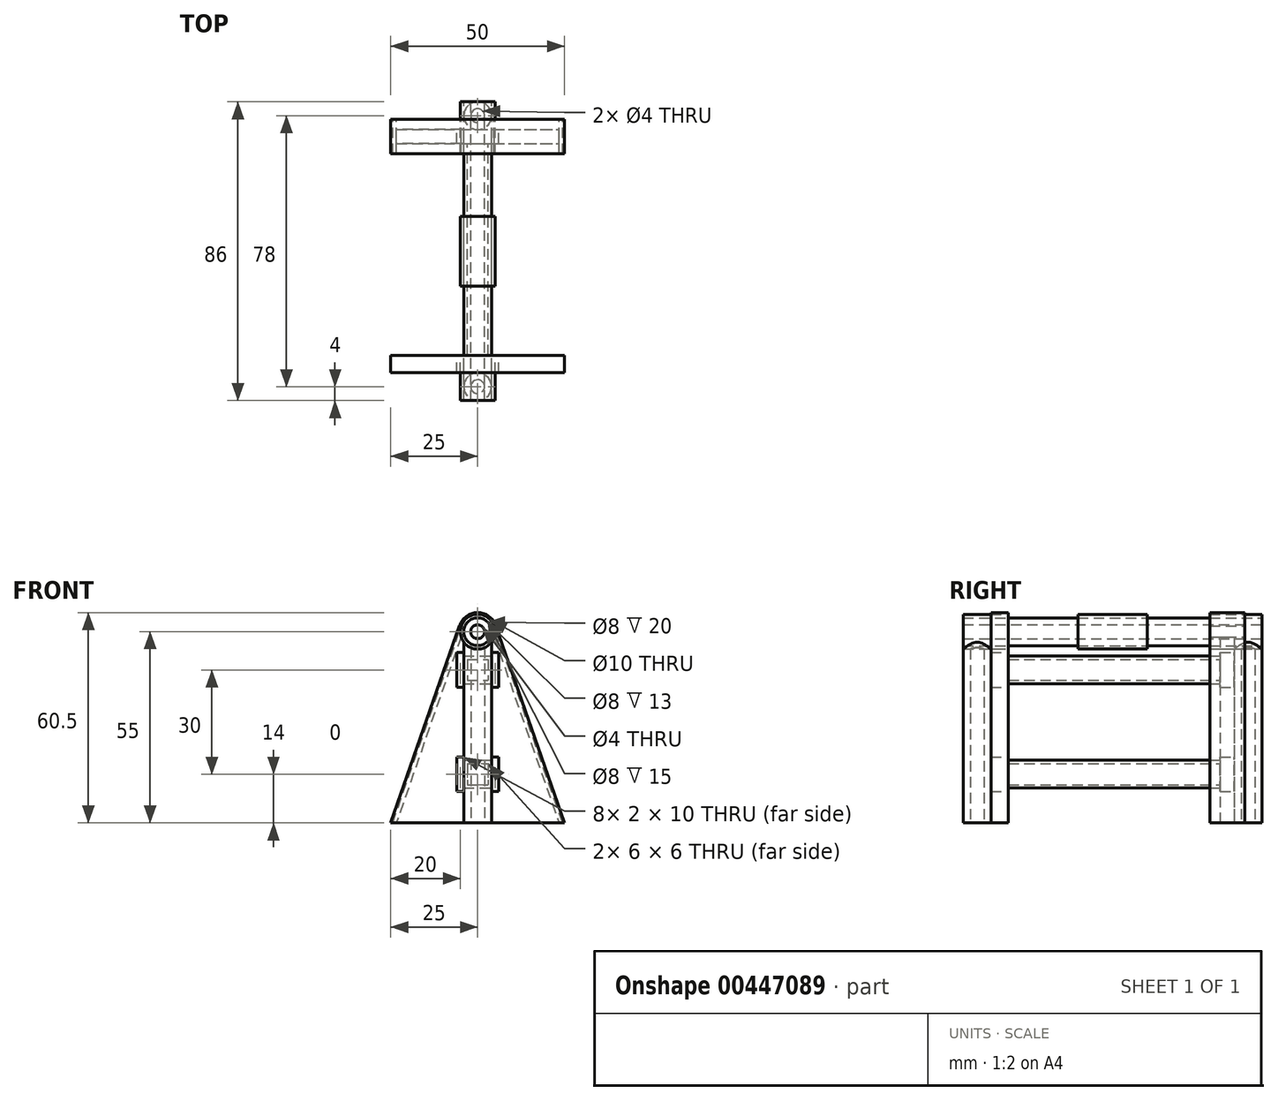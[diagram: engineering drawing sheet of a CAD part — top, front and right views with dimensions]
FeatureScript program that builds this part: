
annotation { "Feature Type Name" : "Feature", "Feature Type Description" : "" }
export const myFeature = defineFeature(function(context is Context, id is Id, definition is map)
    precondition{}
    {
        {
            var Q0;
            Q0=qCreatedBy(makeId("Top.planeOp"),FACE);
            var sketch = newSketch(context, id + "F0", { "sketchPlane" : qUnion([Q0])});
            skCircle(sketch, "E0", {"center": v(0, -4) * mm, "radius": 4 * mm});
            skCircle(sketch, "E1", {"center": v(0, -82) * mm, "radius": 4 * mm});
            skCircle(sketch, "E2", {"center": v(0, -4) * mm, "radius": 2 * mm});
            skCircle(sketch, "E3", {"center": v(0, -82) * mm, "radius": 2 * mm});
            skSolve(sketch);
        }
        {
            var Q0;
            Q0=qCreatedBy(makeId("Front.planeOp"),FACE);
            var sketch = newSketch(context, id + "F1", { "sketchPlane" : qUnion([Q0])});
            skCircle(sketch, "E4", {"center": v(0, 55) * mm, "radius": 4 * mm});
            skCircle(sketch, "E5", {"center": v(0, 55) * mm, "radius": 5 * mm});
            skLineSegment(sketch, "E6", {"start": v(-25, 0) * mm, "end": v(25, 0) * mm});
            skLineSegment(sketch, "E7.bottom", {"start": v(-4, 48) * mm, "end": v(4, 48) * mm});
            skLineSegment(sketch, "E7.top", {"start": v(-4, 40) * mm, "end": v(4, 40) * mm});
            skLineSegment(sketch, "E7.left", {"start": v(-4, 48) * mm, "end": v(-4, 40) * mm});
            skLineSegment(sketch, "E7.right", {"start": v(4, 48) * mm, "end": v(4, 40) * mm});
            skLineSegment(sketch, "E8.bottom", {"start": v(-3, 47) * mm, "end": v(3, 47) * mm});
            skLineSegment(sketch, "E8.top", {"start": v(-3, 41) * mm, "end": v(3, 41) * mm});
            skLineSegment(sketch, "E8.left", {"start": v(-3, 47) * mm, "end": v(-3, 41) * mm});
            skLineSegment(sketch, "E8.right", {"start": v(3, 47) * mm, "end": v(3, 41) * mm});
            skLineSegment(sketch, "E9", {"start": v(3, 41) * mm, "end": v(4, 41) * mm, "construction": true});
            skLineSegment(sketch, "E10", {"start": v(3, 41) * mm, "end": v(3, 40) * mm, "construction": true});
            skPoint(sketch, "E11", {"position": v(0, 44) * mm});
            skLineSegment(sketch, "E12.bottom", {"start": v(-4, 18) * mm, "end": v(4, 18) * mm});
            skLineSegment(sketch, "E12.top", {"start": v(-4, 10) * mm, "end": v(4, 10) * mm});
            skLineSegment(sketch, "E12.left", {"start": v(-4, 18) * mm, "end": v(-4, 10) * mm});
            skLineSegment(sketch, "E12.right", {"start": v(4, 18) * mm, "end": v(4, 10) * mm});
            skLineSegment(sketch, "E13.bottom", {"start": v(-3, 17) * mm, "end": v(3, 17) * mm});
            skLineSegment(sketch, "E13.top", {"start": v(-3, 11) * mm, "end": v(3, 11) * mm});
            skLineSegment(sketch, "E13.left", {"start": v(-3, 17) * mm, "end": v(-3, 11) * mm});
            skLineSegment(sketch, "E13.right", {"start": v(3, 17) * mm, "end": v(3, 11) * mm});
            skLineSegment(sketch, "E14", {"start": v(3, 11) * mm, "end": v(4, 11) * mm, "construction": true});
            skLineSegment(sketch, "E15", {"start": v(3, 11) * mm, "end": v(3, 10) * mm, "construction": true});
            skPoint(sketch, "E16", {"position": v(0, 14) * mm});
            skLineSegment(sketch, "E17", {"start": v(4, 52) * mm, "end": v(4, 0) * mm, "construction": true});
            skLineSegment(sketch, "E18", {"start": v(-4, 52) * mm, "end": v(-4, 0) * mm, "construction": true});
            skCircle(sketch, "E19", {"center": v(0, 55) * mm, "radius": 3 * mm});
            skCircle(sketch, "E20", {"center": v(0, 55) * mm, "radius": 5.5 * mm});
            skLineSegment(sketch, "E21", {"start": v(-25, 0) * mm, "end": v(-5.2, 56.81) * mm});
            skLineSegment(sketch, "E22", {"start": v(25, 0) * mm, "end": v(5.2, 56.81) * mm});
            skLineSegment(sketch, "E23.bottom", {"start": v(-4, 39) * mm, "end": v(-6, 39) * mm});
            skLineSegment(sketch, "E23.top", {"start": v(-4, 49) * mm, "end": v(-6, 49) * mm});
            skLineSegment(sketch, "E23.left", {"start": v(-4, 39) * mm, "end": v(-4, 49) * mm});
            skLineSegment(sketch, "E23.right", {"start": v(-6, 39) * mm, "end": v(-6, 49) * mm});
            skLineSegment(sketch, "E24", {"start": v(0, 55) * mm, "end": v(0, 0) * mm, "construction": true});
            skLineSegment(sketch, "E25.MirrorCS", {"start": v(4, 39) * mm, "end": v(6, 39) * mm});
            skLineSegment(sketch, "E26.MirrorCS", {"start": v(4, 49) * mm, "end": v(6, 49) * mm});
            skLineSegment(sketch, "E27.MirrorCS", {"start": v(6, 39) * mm, "end": v(6, 49) * mm});
            skLineSegment(sketch, "E28.MirrorCS", {"start": v(4, 39) * mm, "end": v(4, 49) * mm});
            skLineSegment(sketch, "E29.bottom", {"start": v(-4, 9) * mm, "end": v(-6, 9) * mm});
            skLineSegment(sketch, "E29.top", {"start": v(-4, 19) * mm, "end": v(-6, 19) * mm});
            skLineSegment(sketch, "E29.left", {"start": v(-4, 9) * mm, "end": v(-4, 19) * mm});
            skLineSegment(sketch, "E29.right", {"start": v(-6, 9) * mm, "end": v(-6, 19) * mm});
            skLineSegment(sketch, "E30.MirrorCS", {"start": v(4, 9) * mm, "end": v(6, 9) * mm});
            skLineSegment(sketch, "E31.MirrorCS", {"start": v(6, 9) * mm, "end": v(6, 19) * mm});
            skLineSegment(sketch, "E32.MirrorCS", {"start": v(4, 19) * mm, "end": v(6, 19) * mm});
            skLineSegment(sketch, "E33.MirrorCS", {"start": v(4, 9) * mm, "end": v(4, 19) * mm});
            skCircle(sketch, "E34", {"center": v(0, 55) * mm, "radius": 2 * mm});
            skLineSegment(sketch, "E35", {"start": v(-24.47, 0) * mm, "end": v(-4.72, 56.65) * mm});
            skLineSegment(sketch, "E36", {"start": v(-4.76, 53.48) * mm, "end": v(-23.41, 0) * mm});
            skLineSegment(sketch, "E37", {"start": v(-17.97, 18.64) * mm, "end": v(-17.03, 18.3) * mm, "construction": true});
            skLineSegment(sketch, "E38.MirrorCS", {"start": v(4.76, 53.48) * mm, "end": v(23.41, 0) * mm});
            skLineSegment(sketch, "E39.MirrorCS", {"start": v(24.47, 0) * mm, "end": v(4.72, 56.65) * mm});
            skSolve(sketch);
        }
        {
            var Q0;
            Q0=makeQuery(id+"F1.imprint","IMPRINT",FACE,{"disambiguationData":[TD([[makeQuery(id+"F1.imprint","IMPRINT",EDGE,{"derivedFrom":sQuery(id+"F1.wireOp",EDGE,"E7.bottom")}),-1.0]])]});
            var Q1;
            Q1=makeQuery(id+"F1.imprint","IMPRINT",FACE,{"disambiguationData":[TD([[makeQuery(id+"F1.imprint","IMPRINT",EDGE,{"derivedFrom":sQuery(id+"F1.wireOp",EDGE,"E12.bottom")}),-1.0]])]});
            var Q2;
            {var subQ5=sQuery(id+"F1.wireOp",EDGE,"E7.top");Q2=makeQuery(id+"F1.imprint","IMPRINT",FACE,{"disambiguationData":[TD([[makeQuery(id+"F1.imprint","IMPRINT",EDGE,{"derivedFrom":subQ5}),1.0]])]});}
            extrude(context, id + "F2", {"entities" : qUnion([Q0, Q1, Q2]), "depth" : 73 * mm, "hasSecondDirection" : true, "secondDirectionOppositeDirection" : false, "secondDirectionDepth" : 12 * mm});
        }
        {
            var Q0;
            Q0=makeQuery(id+"F0.imprint","IMPRINT",FACE,{"disambiguationData":[TD([[makeQuery(id+"F0.imprint","IMPRINT",EDGE,{"derivedFrom":sQuery(id+"F0.wireOp",EDGE,"E2")}),1.0]])]});
            var Q1;
            Q1=makeQuery(id+"F0.imprint","IMPRINT",FACE,{"disambiguationData":[TD([[makeQuery(id+"F0.imprint","IMPRINT",EDGE,{"derivedFrom":sQuery(id+"F0.wireOp",EDGE,"E0")}),1.0]])]});
            var Q2;
            Q2=makeQuery(id+"F0.imprint","IMPRINT",FACE,{"disambiguationData":[TD([[makeQuery(id+"F0.imprint","IMPRINT",EDGE,{"derivedFrom":sQuery(id+"F0.wireOp",EDGE,"E1")}),1.0]])]});
            var Q3;
            Q3=makeQuery(id+"F0.imprint","IMPRINT",FACE,{"disambiguationData":[TD([[makeQuery(id+"F0.imprint","IMPRINT",EDGE,{"derivedFrom":sQuery(id+"F0.wireOp",EDGE,"E3")}),1.0]])]});
            extrude(context, id + "F3", {"entities" : qUnion([Q0, Q1, Q2, Q3]), "operationType" : NewBodyOperationType.REMOVE, "depth" : 50 * mm});
        }
        {
            var Q0;
            Q0=qSketchRegion(id+"F0",true);
            extrude(context, id + "F4", {"entities" : qUnion([Q0]), "depth" : 55 * mm});
        }
        {
            var Q0;
            Q0=makeQuery(id+"F1.imprint","IMPRINT",FACE,{"disambiguationData":[TD([[makeQuery(id+"F1.imprint","IMPRINT",EDGE,{"derivedFrom":sQuery(id+"F1.wireOp",EDGE,"E4")}),1.0]])]});
            var Q1;
            Q1=makeQuery(id+"F1.imprint","IMPRINT",FACE,{"disambiguationData":[TD([[makeQuery(id+"F1.imprint","IMPRINT",EDGE,{"derivedFrom":sQuery(id+"F1.wireOp",EDGE,"E4")}),-1.0]])]});
            var Q2;
            Q2=makeQuery(id+"F1.imprint","IMPRINT",FACE,{"disambiguationData":[TD([[makeQuery(id+"F1.imprint","IMPRINT",EDGE,{"derivedFrom":sQuery(id+"F1.wireOp",EDGE,"E19")}),1.0]])]});
            var Q3;
            Q3=makeQuery(id+"F1.imprint","IMPRINT",FACE,{"disambiguationData":[TD([[makeQuery(id+"F1.imprint","IMPRINT",EDGE,{"derivedFrom":sQuery(id+"F1.wireOp",EDGE,"E34")}),1.0]])]});
            extrude(context, id + "F5", {"entities" : qUnion([Q0, Q1, Q2, Q3]), "operationType" : NewBodyOperationType.REMOVE, "depth" : 120 * mm});
        }
        {
            var Q0;
            Q0=makeQuery(id+"F1.imprint","IMPRINT",FACE,{"disambiguationData":[TD([[makeQuery(id+"F1.imprint","IMPRINT",EDGE,{"derivedFrom":sQuery(id+"F1.wireOp",EDGE,"E4")}),-1.0]])]});
            extrude(context, id + "F6", {"entities" : qUnion([Q0]), "depth" : 15 * mm});
        }
        {
            var Q0;
            Q0=makeQuery(id+"F1.imprint","IMPRINT",FACE,{"disambiguationData":[TD([[makeQuery(id+"F1.imprint","IMPRINT",EDGE,{"derivedFrom":sQuery(id+"F1.wireOp",EDGE,"E4")}),-1.0]])]});
            var Q1;
            {var subQ0=sQuery(id+"F1.wireOp",EDGE,"NSQy4Wvw-krST-z6iW-aOdV-dfbufY4ojtwf");Q1=makeQuery(id+"F1.imprint","IMPRINT",FACE,{"disambiguationData":[TD([[makeQuery(id+"F1.imprint","IMPRINT",EDGE,{"derivedFrom":subQ0}),1.0]])]});}
            var Q2;
            {var subQ0=sQuery(id+"F1.wireOp",EDGE,"pC06kpPF-Ja5L-Bko1-UVUB-2QjUFd2QXtQQ");Q2=makeQuery(id+"F1.imprint","IMPRINT",FACE,{"disambiguationData":[TD([[makeQuery(id+"F1.imprint","IMPRINT",EDGE,{"derivedFrom":subQ0}),1.0]])]});}
            extrude(context, id + "F7", {"entities" : qUnion([Q0, Q1, Q2]), "depth" : 86 * mm, "hasSecondDirection" : true, "secondDirectionOppositeDirection" : false, "secondDirectionDepth" : 73 * mm});
        }
        {
            var Q0;
            Q0=makeQuery(id+"F1.imprint","IMPRINT",FACE,{"disambiguationData":[TD([[makeQuery(id+"F1.imprint","IMPRINT",EDGE,{"derivedFrom":sQuery(id+"F1.wireOp",EDGE,"E4")}),1.0]])]});
            var Q1;
            Q1=makeQuery(id+"F1.imprint","IMPRINT",FACE,{"disambiguationData":[TD([[makeQuery(id+"F1.imprint","IMPRINT",EDGE,{"derivedFrom":sQuery(id+"F1.wireOp",EDGE,"E19")}),1.0]])]});
            extrude(context, id + "F8", {"entities" : qUnion([Q0, Q1]), "depth" : 86 * mm});
        }
        {
            var Q0;
            {var subQ6=sQuery(id+"F1.wireOp",EDGE,"E7.bottom");Q0=makeQuery(id+"F1.imprint","IMPRINT",FACE,{"disambiguationData":[TD([[makeQuery(id+"F1.imprint","IMPRINT",EDGE,{"derivedFrom":subQ6}),1.0]])]});}
            var Q1;
            {var subQ0=sQuery(id+"F1.wireOp",EDGE,"E36");var subQ1=sQuery(id+"F1.wireOp",EDGE,"E5");var subQ2=makeQuery(id+"F1.imprint","INTERSECT",VERTEX,{"derivedFrom":[subQ1,subQ0]});Q1=makeQuery(id+"F1.imprint","IMPRINT",FACE,{"disambiguationData":[TD([[makeQuery(id+"F1.imprint","IMPRINT",EDGE,{"disambiguationData":[TD([[subQ2,-1.0]])],"derivedFrom":subQ1}),-1.0]])]});}
            var Q2;
            {var subQ1=sQuery(id+"F1.wireOp",EDGE,"E7.bottom");Q2=makeQuery(id+"F1.imprint","IMPRINT",FACE,{"disambiguationData":[TD([[makeQuery(id+"F1.imprint","IMPRINT",EDGE,{"derivedFrom":subQ1}),-1.0]])]});}
            var Q3;
            Q3=makeQuery(id+"F1.imprint","IMPRINT",FACE,{"disambiguationData":[TD([[makeQuery(id+"F1.imprint","IMPRINT",EDGE,{"derivedFrom":sQuery(id+"F1.wireOp",EDGE,"E8.bottom")}),-1.0]])]});
            var Q4;
            Q4=makeQuery(id+"F1.imprint","IMPRINT",FACE,{"disambiguationData":[TD([[makeQuery(id+"F1.imprint","IMPRINT",EDGE,{"derivedFrom":sQuery(id+"F1.wireOp",EDGE,"E13.bottom")}),-1.0]])]});
            var Q5;
            {var subQ1=sQuery(id+"F1.wireOp",EDGE,"E12.bottom");Q5=makeQuery(id+"F1.imprint","IMPRINT",FACE,{"disambiguationData":[TD([[makeQuery(id+"F1.imprint","IMPRINT",EDGE,{"derivedFrom":subQ1}),-1.0]])]});}
            extrude(context, id + "F9", {"entities" : qUnion([Q0, Q1, Q2, Q3, Q4, Q5]), "depth" : 12 * mm, "hasSecondDirection" : true, "secondDirectionOppositeDirection" : false, "secondDirectionDepth" : 8 * mm});
        }
        {
            var Q0;
            {var subQ1=sQuery(id+"F1.wireOp",EDGE,"E7.bottom");Q0=makeQuery(id+"F1.imprint","IMPRINT",FACE,{"disambiguationData":[TD([[makeQuery(id+"F1.imprint","IMPRINT",EDGE,{"derivedFrom":subQ1}),-1.0]])]});}
            var Q1;
            Q1=makeQuery(id+"F1.imprint","IMPRINT",FACE,{"disambiguationData":[TD([[makeQuery(id+"F1.imprint","IMPRINT",EDGE,{"derivedFrom":sQuery(id+"F1.wireOp",EDGE,"E6")}),1.0]])]});
            var Q2;
            Q2=makeQuery(id+"F1.imprint","IMPRINT",FACE,{"disambiguationData":[TD([[makeQuery(id+"F1.imprint","IMPRINT",EDGE,{"derivedFrom":sQuery(id+"F1.wireOp",EDGE,"E5")}),-1.0]])]});
            var Q3;
            {var subQ2=sQuery(id+"F1.wireOp",EDGE,"E35");var subQ4=sQuery(id+"F1.wireOp",EDGE,"E5");var subQ5=makeQuery(id+"F1.imprint","INTERSECT",VERTEX,{"derivedFrom":[subQ4,subQ2]});Q3=makeQuery(id+"F1.imprint","IMPRINT",FACE,{"disambiguationData":[TD([[makeQuery(id+"F1.imprint","IMPRINT",EDGE,{"disambiguationData":[TD([[subQ5,1.0]])],"derivedFrom":subQ4}),-1.0]])]});}
            var Q4;
            {var subQ6=sQuery(id+"F1.wireOp",EDGE,"E7.bottom");Q4=makeQuery(id+"F1.imprint","IMPRINT",FACE,{"disambiguationData":[TD([[makeQuery(id+"F1.imprint","IMPRINT",EDGE,{"derivedFrom":subQ6}),1.0]])]});}
            var Q5;
            Q5=makeQuery(id+"F1.imprint","IMPRINT",FACE,{"disambiguationData":[TD([[makeQuery(id+"F1.imprint","IMPRINT",EDGE,{"derivedFrom":sQuery(id+"F1.wireOp",EDGE,"E8.bottom")}),-1.0]])]});
            var Q6;
            Q6=makeQuery(id+"F1.imprint","IMPRINT",FACE,{"disambiguationData":[TD([[makeQuery(id+"F1.imprint","IMPRINT",EDGE,{"derivedFrom":sQuery(id+"F1.wireOp",EDGE,"E13.bottom")}),-1.0]])]});
            var Q7;
            {var subQ1=sQuery(id+"F1.wireOp",EDGE,"E12.bottom");Q7=makeQuery(id+"F1.imprint","IMPRINT",FACE,{"disambiguationData":[TD([[makeQuery(id+"F1.imprint","IMPRINT",EDGE,{"derivedFrom":subQ1}),-1.0]])]});}
            extrude(context, id + "F10", {"entities" : qUnion([Q0, Q1, Q2, Q3, Q4, Q5, Q6, Q7]), "depth" : 78 * mm, "hasSecondDirection" : true, "secondDirectionOppositeDirection" : false, "secondDirectionDepth" : 73 * mm});
        }
        {
            var Q0;
            Q0=makeQuery(id+"F1.imprint","IMPRINT",FACE,{"disambiguationData":[TD([[makeQuery(id+"F1.imprint","IMPRINT",EDGE,{"derivedFrom":sQuery(id+"F1.wireOp",EDGE,"E4")}),-1.0]])]});
            extrude(context, id + "F11", {"entities" : qUnion([Q0]), "depth" : 53 * mm, "hasSecondDirection" : true, "secondDirectionOppositeDirection" : false, "secondDirectionDepth" : 33 * mm});
        }
        {
            var Q0;
            {var subQ0=sQuery(id+"F1.wireOp",EDGE,"E35");var subQ1=sQuery(id+"F1.wireOp",EDGE,"E6");var subQ2=makeQuery(id+"F1.imprint","INTERSECT",VERTEX,{"derivedFrom":[subQ1,subQ0]});Q0=makeQuery(id+"F1.imprint","IMPRINT",FACE,{"disambiguationData":[TD([[makeQuery(id+"F1.imprint","IMPRINT",EDGE,{"disambiguationData":[TD([[subQ2,-1.0]])],"derivedFrom":subQ1}),1.0]])]});}
            var Q1;
            {var subQ0=sQuery(id+"F1.wireOp",EDGE,"E38.MirrorCS");var subQ1=sQuery(id+"F1.wireOp",EDGE,"E6");var subQ2=makeQuery(id+"F1.imprint","INTERSECT",VERTEX,{"derivedFrom":[subQ1,subQ0]});Q1=makeQuery(id+"F1.imprint","IMPRINT",FACE,{"disambiguationData":[TD([[makeQuery(id+"F1.imprint","IMPRINT",EDGE,{"disambiguationData":[TD([[subQ2,-1.0]])],"derivedFrom":subQ1}),1.0]])]});}
            var Q2;
            {var subQ0=sQuery(id+"F1.wireOp",EDGE,"E38.MirrorCS");var subQ1=sQuery(id+"F1.wireOp",EDGE,"E5");var subQ2=makeQuery(id+"F1.imprint","INTERSECT",VERTEX,{"derivedFrom":[subQ1,subQ0]});Q2=makeQuery(id+"F1.imprint","IMPRINT",FACE,{"disambiguationData":[TD([[makeQuery(id+"F1.imprint","IMPRINT",EDGE,{"disambiguationData":[TD([[subQ2,-1.0]])],"derivedFrom":subQ1}),-1.0]])]});}
            var Q3;
            {var subQ0=sQuery(id+"F1.wireOp",EDGE,"E35");var subQ1=sQuery(id+"F1.wireOp",EDGE,"E5");var subQ2=makeQuery(id+"F1.imprint","INTERSECT",VERTEX,{"derivedFrom":[subQ1,subQ0]});Q3=makeQuery(id+"F1.imprint","IMPRINT",FACE,{"disambiguationData":[TD([[makeQuery(id+"F1.imprint","IMPRINT",EDGE,{"disambiguationData":[TD([[subQ2,-1.0]])],"derivedFrom":subQ1}),-1.0]])]});}
            extrude(context, id + "F12", {"entities" : qUnion([Q0, Q1, Q2, Q3]), "depth" : 15 * mm, "hasSecondDirection" : true, "secondDirectionOppositeDirection" : false, "secondDirectionDepth" : 5 * mm});
        }
        {
            var Q0;
            {var subQ0=sQuery(id+"F1.wireOp",EDGE,"E22");Q0=makeQuery(id+"F1.imprint","IMPRINT",FACE,{"disambiguationData":[TD([[makeQuery(id+"F1.imprint","IMPRINT",EDGE,{"derivedFrom":subQ0}),1.0]])]});}
            var Q1;
            {var subQ2=sQuery(id+"F1.wireOp",EDGE,"E35");var subQ4=sQuery(id+"F1.wireOp",EDGE,"E5");var subQ5=makeQuery(id+"F1.imprint","INTERSECT",VERTEX,{"derivedFrom":[subQ4,subQ2]});Q1=makeQuery(id+"F1.imprint","IMPRINT",FACE,{"disambiguationData":[TD([[makeQuery(id+"F1.imprint","IMPRINT",EDGE,{"disambiguationData":[TD([[subQ5,1.0]])],"derivedFrom":subQ4}),-1.0]])]});}
            var Q2;
            {var subQ0=sQuery(id+"F1.wireOp",EDGE,"E21");Q2=makeQuery(id+"F1.imprint","IMPRINT",FACE,{"disambiguationData":[TD([[makeQuery(id+"F1.imprint","IMPRINT",EDGE,{"derivedFrom":subQ0}),-1.0]])]});}
            extrude(context, id + "F13", {"entities" : qUnion([Q0, Q1, Q2]), "depth" : 15 * mm, "hasSecondDirection" : true, "secondDirectionOppositeDirection" : false, "secondDirectionDepth" : 5 * mm});
        }
    });
